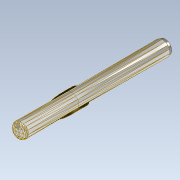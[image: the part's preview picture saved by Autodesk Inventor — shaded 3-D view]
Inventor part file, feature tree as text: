
AUTODESK INVENTOR PART (.ipt)
format: ipt  version: 2022 (Build 260153000, 153)  size: 1,195,008 bytes
history: native  units: in
note: dims shown in document units (in); Inventor stores cm internally (conversion verified against a paired STEP export)
features: other x3, extrude x2, sketch x2, plane x1, projected_geometry x1
ambient origin geometry x8: Origin, YZ Plane, XZ Plane, XY Plane, X Axis, Y Axis, Z Axis, Center Point
bodies: Solid1 (feature_tree)
feature tree (9):
  other  "boquilla_flauta"
  plane  "Work Plane1"
  extrude  "Extrusion1"  Depth=0.1in TaperAngle=0.0deg
  extrude  "Extrusion2"  [1 undecoded]
  sketch  "Sketch1"  dims[d0=0.1in d1=0.0in d2=5.4125in d3=0.0in]
  sketch  "Sketch2"
  projected_geometry  "Projected Loop1"
  other  "MeshFeature1"
  other  "Srf1"
note: 1 required parameter value undecoded (feature->parameter linkage not recoverable at this tier; creation-order binding heuristic only, values carry confidence <= 0.55)
